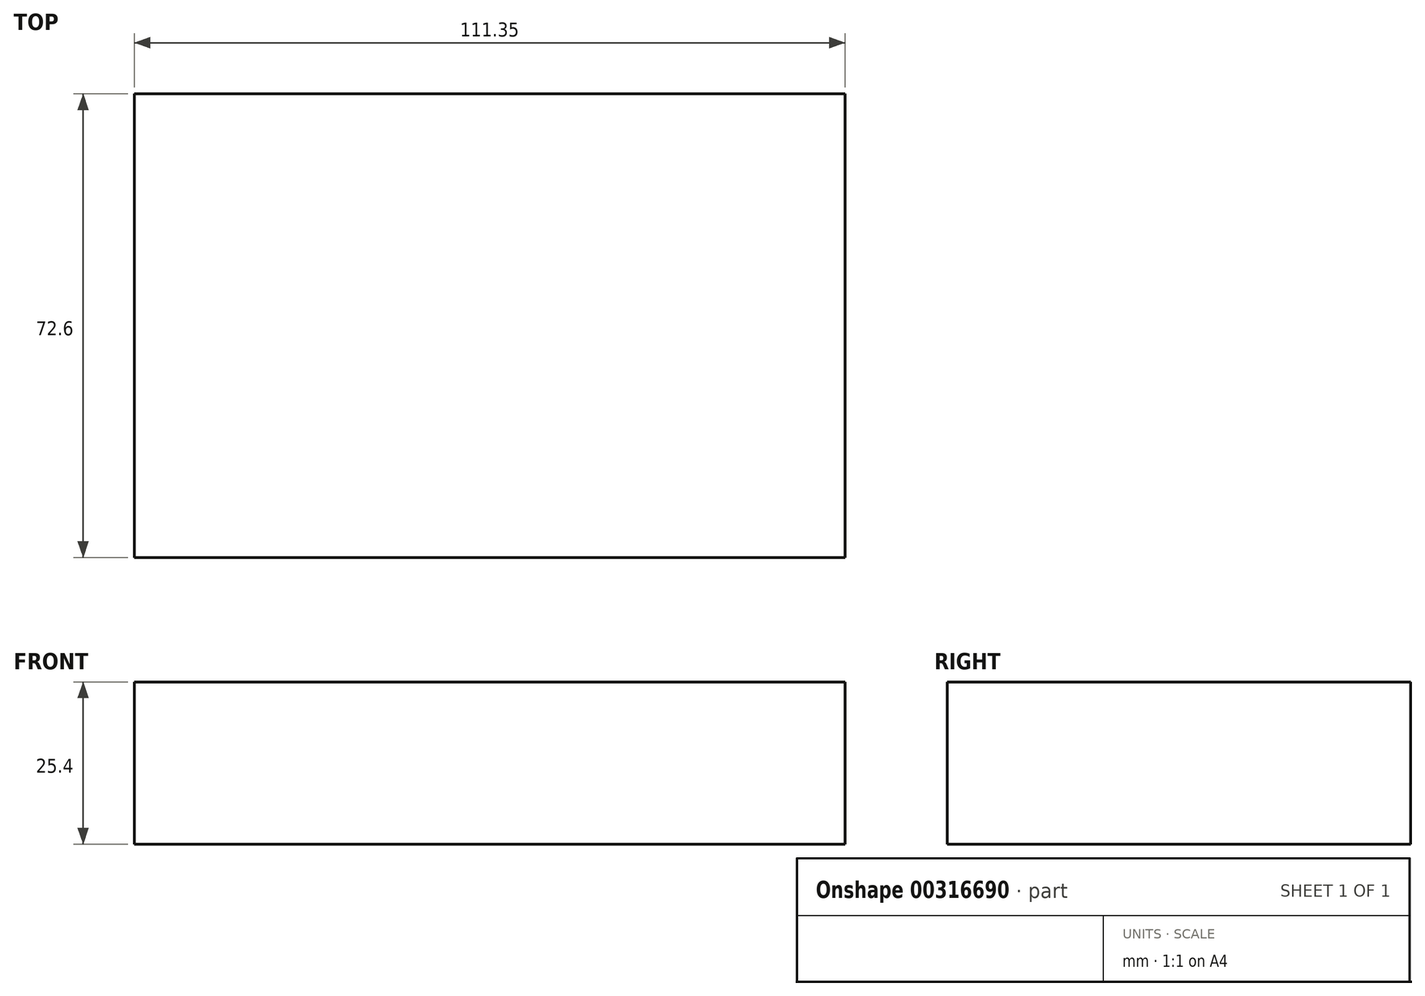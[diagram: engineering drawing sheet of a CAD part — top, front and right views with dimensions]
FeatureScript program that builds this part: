
annotation { "Feature Type Name" : "Feature", "Feature Type Description" : "" }
export const myFeature = defineFeature(function(context is Context, id is Id, definition is map)
    precondition{}
    {
        {
            var Q0;
            Q0=qCreatedBy(makeId("Top.planeOp"),FACE);
            var sketch = newSketch(context, id + "F0", { "sketchPlane" : qUnion([Q0])});
            skLineSegment(sketch, "E0.bottom", {"start": v(-55.03, -14.23) * mm, "end": v(56.32, -14.23) * mm});
            skLineSegment(sketch, "E0.top", {"start": v(-55.03, 58.37) * mm, "end": v(56.32, 58.37) * mm});
            skLineSegment(sketch, "E0.left", {"start": v(-55.03, -14.23) * mm, "end": v(-55.03, 58.37) * mm});
            skLineSegment(sketch, "E0.right", {"start": v(56.32, -14.23) * mm, "end": v(56.32, 58.37) * mm});
            skSolve(sketch);
        }
        {
            var Q0;
            Q0 = qSketchRegion(id + "F0", true);
            extrude(context, id + "F1", {"entities" : qUnion([Q0]), "depth" : 25.4 * mm});
        }
    });
